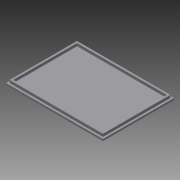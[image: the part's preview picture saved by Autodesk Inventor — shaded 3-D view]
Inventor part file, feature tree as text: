
AUTODESK INVENTOR PART (.ipt)
format: ipt  version: 2013 (Build 170138000, 138)  size: 88,576 bytes
history: native  units: mm
features: extrude x2, sketch x2
ambient origin geometry x8: Origin, YZ Plane, XZ Plane, XY Plane, X Axis, Y Axis, Z Axis, Center Point
bodies: Solid1 (feature_tree)
feature tree (4):
  extrude  "Extrusion1"  Depth=78.6mm
  extrude  "Extrusion2"  Depth=2.0mm
  sketch  "Sketch1"  dims[d0=107.3mm d1=78.6mm]
  sketch  "Sketch2"  dims[d2=2.0mm d3=0.0mm d4=2.0mm d5=2.0mm d6=3.0mm d7=0.0mm]
